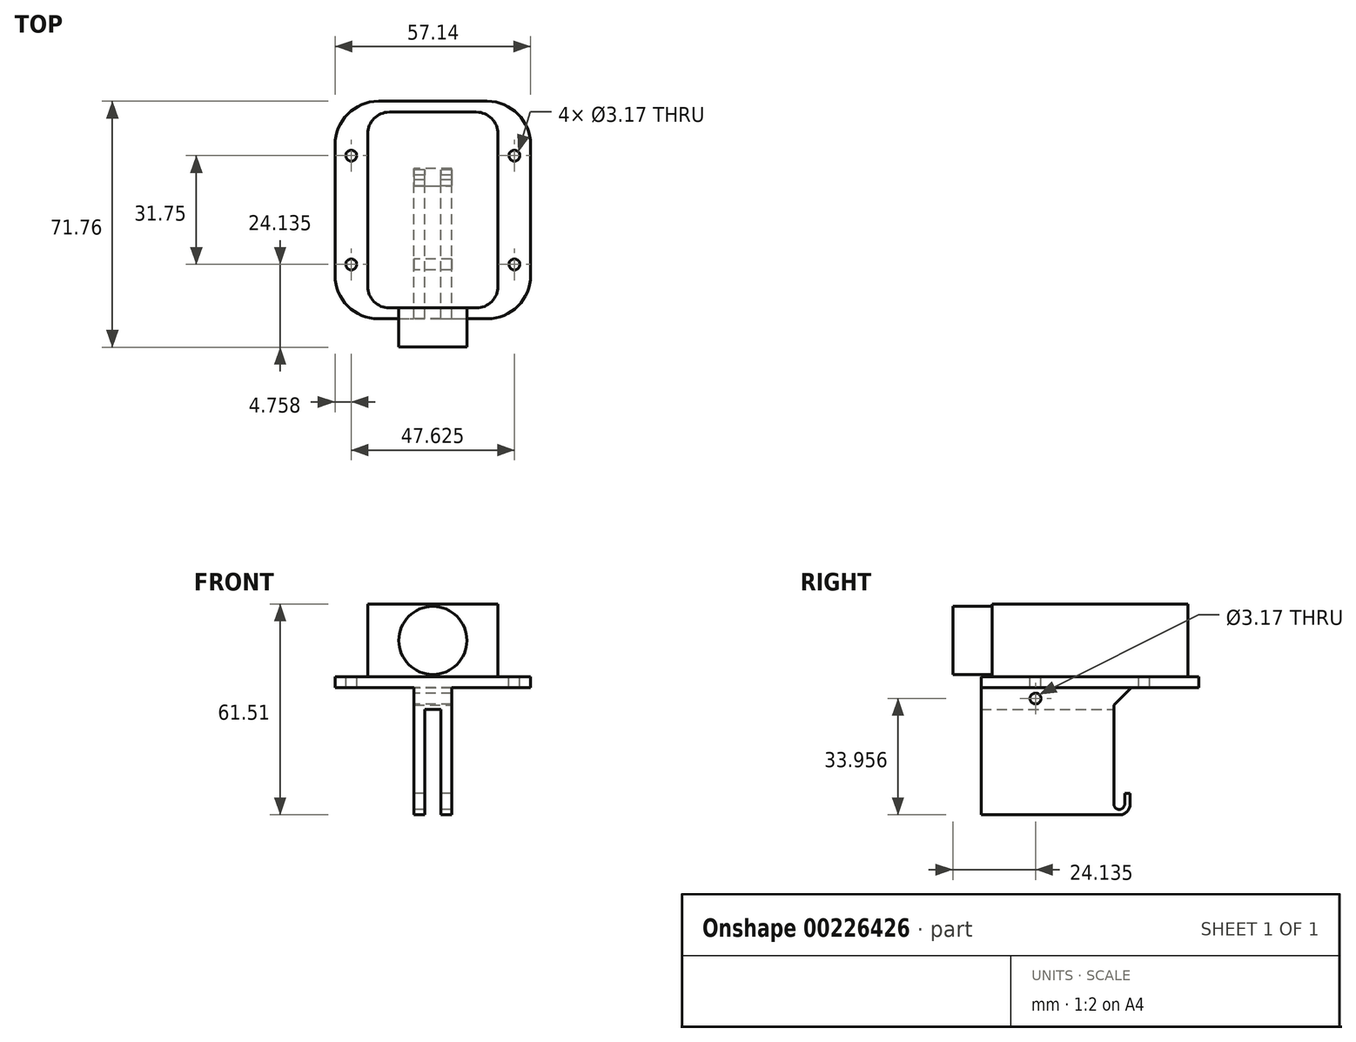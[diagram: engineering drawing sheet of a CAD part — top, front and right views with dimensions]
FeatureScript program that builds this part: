
annotation { "Feature Type Name" : "Feature", "Feature Type Description" : "" }
export const myFeature = defineFeature(function(context is Context, id is Id, definition is map)
    precondition{}
    {
        {
            var Q0;
            Q0=qCreatedBy(makeId("Top.planeOp"),FACE);
            var sketch = newSketch(context, id + "F0", { "sketchPlane" : qUnion([Q0])});
            skLineSegment(sketch, "E0.bottom", {"start": v(-12.7, 28.58) * mm, "end": v(12.7, 28.58) * mm});
            skLineSegment(sketch, "E0.top", {"start": v(-12.7, -28.58) * mm, "end": v(12.7, -28.58) * mm});
            skLineSegment(sketch, "E0.left", {"start": v(-19.05, 22.23) * mm, "end": v(-19.05, -22.23) * mm});
            skLineSegment(sketch, "E0.right", {"start": v(19.05, 22.23) * mm, "end": v(19.05, -22.23) * mm});
            skPoint(sketch, "E0.middle", {"position": v(0, 0) * mm});
            skPoint(sketch, "E1.visualSharp", {"position": v(-19.05, 28.58) * mm});
            skArc(sketch, "E1.filletArc", {"start": v(-12.7, 28.58) * mm, "mid": v(-17.2, 26.72) * mm, "end": v(-19.05, 22.23) * mm});
            skPoint(sketch, "E2.visualSharp", {"position": v(19.05, 28.58) * mm});
            skArc(sketch, "E2.filletArc", {"start": v(19.05, 22.23) * mm, "mid": v(17.2, 26.72) * mm, "end": v(12.7, 28.58) * mm});
            skPoint(sketch, "E3.visualSharp", {"position": v(19.05, -28.58) * mm});
            skArc(sketch, "E3.filletArc", {"start": v(12.7, -28.58) * mm, "mid": v(17.2, -26.72) * mm, "end": v(19.05, -22.23) * mm});
            skPoint(sketch, "E4.visualSharp", {"position": v(-19.05, -28.58) * mm});
            skArc(sketch, "E4.filletArc", {"start": v(-19.05, -22.23) * mm, "mid": v(-17.2, -26.72) * mm, "end": v(-12.7, -28.58) * mm});
            skCircle(sketch, "E5", {"center": v(0, 19.05) * mm, "radius": 4.76 * mm});
            skCircle(sketch, "E6", {"center": v(0, 8.57) * mm, "radius": 2.98 * mm});
            skSolve(sketch);
        }
        {
            var Q0;
            Q0 = qSketchRegion(id + "F0", true);
            var Q1;
            Q1=makeQuery(id+"F0.imprint","IMPRINT",FACE,{"disambiguationData":[TD([[makeQuery(id+"F0.imprint","IMPRINT",EDGE,{"derivedFrom":sQuery(id+"F0.wireOp",EDGE,"E5")}),1.0]])]});
            var Q2;
            Q2=makeQuery(id+"F0.imprint","IMPRINT",FACE,{"disambiguationData":[TD([[makeQuery(id+"F0.imprint","IMPRINT",EDGE,{"derivedFrom":sQuery(id+"F0.wireOp",EDGE,"E6")}),1.0]])]});
            extrude(context, id + "F1", {"entities" : qUnion([Q0, Q1, Q2]), "depth" : 21.2 * mm, "offsetDistance" : 25.4 * mm, "symmetric" : true});
        }
        {
            var Q0;
            Q0=makeQuery(id+"F1.opExtrude","SWEPT_FACE",FACE,{"disambiguationData":[OSD([sQuery(id+"F0.wireOp",EDGE,"E0.top")])]});
            var sketch = newSketch(context, id + "F2", { "sketchPlane" : qUnion([Q0])});
            skCircle(sketch, "E7", {"center": v(0, 0) * mm, "radius": 9.94 * mm});
            skSolve(sketch);
        }
        {
            var Q0;
            Q0 = qSketchRegion(id + "F2", true);
            extrude(context, id + "F3", {"entities" : qUnion([Q0]), "operationType" : NewBodyOperationType.ADD, "depth" : 11.43 * mm, "offsetDistance" : 25.4 * mm});
        }
        {
            var Q0;
            Q0=qCreatedBy(makeId("Front.planeOp"),FACE);
            var sketch = newSketch(context, id + "F4", { "sketchPlane" : qUnion([Q0])});
            skLineSegment(sketch, "E8.bottom", {"start": v(-2.29, -13.78) * mm, "end": v(2.29, -13.78) * mm});
            skLineSegment(sketch, "E8.left", {"start": v(-2.29, -13.78) * mm, "end": v(-2.29, -51.88) * mm});
            skLineSegment(sketch, "E8.right", {"start": v(2.29, -13.78) * mm, "end": v(2.29, -51.88) * mm});
            skPoint(sketch, "E8.middle", {"position": v(0, -32.83) * mm});
            skLineSegment(sketch, "E9.bottom", {"start": v(-28.57, -10.6) * mm, "end": v(28.57, -10.6) * mm});
            skLineSegment(sketch, "E9.top", {"start": v(-28.57, -13.78) * mm, "end": v(28.57, -13.78) * mm});
            skLineSegment(sketch, "E9.left", {"start": v(-28.57, -10.6) * mm, "end": v(-28.57, -13.78) * mm});
            skLineSegment(sketch, "E9.right", {"start": v(28.57, -10.6) * mm, "end": v(28.57, -13.78) * mm});
            skPoint(sketch, "E9.middle", {"position": v(0, -12.2) * mm});
            skSolve(sketch);
        }
        {
            var Q0;
            Q0 = qSketchRegion(id + "F4", true);
            extrude(context, id + "F5", {"entities" : qUnion([Q0]), "depth" : 63.5 * mm, "offsetDistance" : 25.4 * mm, "symmetric" : true});
        }
        {
            var Q0;
            Q0=makeQuery(id+"F5.opExtrude","SWEPT_FACE",FACE,{"disambiguationData":[OSD([sQuery(id+"F4.wireOp",EDGE,"E9.bottom")])]});
            var sketch = newSketch(context, id + "F6", { "sketchPlane" : qUnion([Q0])});
            skCircle(sketch, "E10", {"center": v(23.81, 15.88) * mm, "radius": 1.59 * mm});
            skLineSegment(sketch, "E11", {"start": v(28.57, 15.88) * mm, "end": v(19.05, 15.88) * mm, "construction": true});
            skCircle(sketch, "E12.MirrorC", {"center": v(-23.81, 15.88) * mm, "radius": 1.59 * mm});
            skCircle(sketch, "E13.MirrorC", {"center": v(-23.81, -15.88) * mm, "radius": 1.59 * mm});
            skCircle(sketch, "E14.MirrorC", {"center": v(23.81, -15.88) * mm, "radius": 1.59 * mm});
            skSolve(sketch);
        }
        {
            var Q0;
            Q0 = qSketchRegion(id + "F6", true);
            var Q1;
            Q1=makeQuery(id+"F5.opExtrude","SWEPT_FACE",FACE,{"disambiguationData":[OSD([sQuery(id+"F4.wireOp",EDGE,"E9.top")])]});
            extrude(context, id + "F7", {"entities" : qUnion([Q0]), "operationType" : NewBodyOperationType.REMOVE, "endBound" : BoundingType.UP_TO_SURFACE, "oppositeDirection" : true, "depth" : 25.4 * mm, "endBoundEntityFace" : qUnion([Q1]), "offsetDistance" : 25.4 * mm});
        }
        {
            var Q0;
            Q0=qCreatedBy(makeId("Front.planeOp"),FACE);
            var sketch = newSketch(context, id + "F8", { "sketchPlane" : qUnion([Q0])});
            skLineSegment(sketch, "E15.bottom", {"start": v(-2.29, -13.78) * mm, "end": v(2.29, -13.78) * mm});
            skLineSegment(sketch, "E15.left", {"start": v(-2.29, -13.78) * mm, "end": v(-2.29, -50.91) * mm});
            skLineSegment(sketch, "E15.right", {"start": v(2.29, -13.78) * mm, "end": v(2.29, -50.91) * mm});
            skPoint(sketch, "E15.middle", {"position": v(0, -32.35) * mm});
            skLineSegment(sketch, "E16.bottom", {"start": v(-2.29, -50.91) * mm, "end": v(-5.46, -50.91) * mm});
            skLineSegment(sketch, "E16.top", {"start": v(-2.29, -13.78) * mm, "end": v(-5.46, -13.78) * mm});
            skLineSegment(sketch, "E16.left", {"start": v(-2.29, -50.91) * mm, "end": v(-2.29, -13.78) * mm});
            skLineSegment(sketch, "E16.right", {"start": v(-5.46, -50.91) * mm, "end": v(-5.46, -13.78) * mm});
            skLineSegment(sketch, "E17.MirrorCS", {"start": v(5.46, -50.91) * mm, "end": v(5.46, -13.78) * mm});
            skLineSegment(sketch, "E18.MirrorCS", {"start": v(2.29, -50.91) * mm, "end": v(5.46, -50.91) * mm});
            skLineSegment(sketch, "E19.MirrorCS", {"start": v(2.29, -13.78) * mm, "end": v(5.46, -13.78) * mm});
            skLineSegment(sketch, "E20.bottom", {"start": v(5.46, -13.78) * mm, "end": v(-5.46, -13.78) * mm});
            skLineSegment(sketch, "E20.top", {"start": v(5.46, -20.13) * mm, "end": v(-5.46, -20.13) * mm});
            skLineSegment(sketch, "E20.left", {"start": v(5.46, -13.78) * mm, "end": v(5.46, -20.13) * mm});
            skLineSegment(sketch, "E20.right", {"start": v(-5.46, -13.78) * mm, "end": v(-5.46, -20.13) * mm});
            skPoint(sketch, "E20.middle", {"position": v(0, -16.95) * mm});
            skSolve(sketch);
        }
        {
            var Q0;
            Q0 = qSketchRegion(id + "F8", true);
            var Q1;
            Q1=makeQuery(id+"F5.opExtrude","CAP_FACE",FACE,{"disambiguationData":[OSD([sQuery(id+"F4.wireOp",EDGE,"E9.bottom"),sQuery(id+"F4.wireOp",EDGE,"E9.top"),sQuery(id+"F4.wireOp",EDGE,"E9.left"),sQuery(id+"F4.wireOp",EDGE,"E9.right")])],"isStart":false});
            extrude(context, id + "F9", {"entities" : qUnion([Q0]), "operationType" : NewBodyOperationType.ADD, "endBound" : BoundingType.UP_TO_SURFACE, "depth" : 34.92 * mm, "endBoundEntityFace" : qUnion([Q1]), "offsetDistance" : 25.4 * mm, "hasSecondDirection" : true, "secondDirectionOppositeDirection" : true, "secondDirectionDepth" : 12.7 * mm});
        }
        {
            var Q0;
            Q0=makeQuery(id+"F9.opExtrude","SWEPT_FACE",FACE,{"disambiguationData":[OSD([sQuery(id+"F8.wireOp",EDGE,"E16.right")])]});
            var sketch = newSketch(context, id + "F10", { "sketchPlane" : qUnion([Q0])});
            skLineSegment(sketch, "E21", {"start": v(-6.99, -20.13) * mm, "end": v(-6.99, -49.34) * mm});
            skArc(sketch, "E22", {"start": v(-10.16, -47.75) * mm, "mid": v(-8.57, -49.34) * mm, "end": v(-6.99, -47.75) * mm});
            skLineSegment(sketch, "E23", {"start": v(-6.99, -49.34) * mm, "end": v(-11.32, -49.34) * mm});
            skArc(sketch, "E24", {"start": v(-11.75, -47.75) * mm, "mid": v(-6.99, -50.5) * mm, "end": v(-6.99, -45) * mm});
            skLineSegment(sketch, "E25", {"start": v(-10.16, -47.75) * mm, "end": v(-10.16, -44.58) * mm});
            skLineSegment(sketch, "E26", {"start": v(-11.75, -47.75) * mm, "end": v(-11.75, -44.58) * mm});
            skLineSegment(sketch, "E27", {"start": v(-10.16, -44.58) * mm, "end": v(-11.75, -44.58) * mm});
            skLineSegment(sketch, "E28.0", {"start": v(-12.7, -50.91) * mm, "end": v(-12.7, -50.91) * mm});
            skLineSegment(sketch, "E29.0", {"start": v(31.75, -13.78) * mm, "end": v(-31.75, -13.78) * mm});
            skLineSegment(sketch, "E30", {"start": v(-6.99, -20.13) * mm, "end": v(-6.99, -13.78) * mm});
            skLineSegment(sketch, "E31.0", {"start": v(-12.7, -50.91) * mm, "end": v(-12.7, -13.78) * mm});
            skLineSegment(sketch, "E32.0", {"start": v(14.29, -10.6) * mm, "end": v(17.46, -10.6) * mm});
            skCircle(sketch, "E33", {"center": v(15.88, -16.95) * mm, "radius": 1.59 * mm});
            skPoint(sketch, "E33.centerSnap0", {"position": v(15.88, -10.6) * mm});
            skSolve(sketch);
        }
        {
            var Q0;
            {var subQ6=sQuery(id+"F10.wireOp",EDGE,"E25");Q0=makeQuery(id+"F10.imprint","IMPRINT",FACE,{"disambiguationData":[TD([[makeQuery(id+"F10.imprint","IMPRINT",EDGE,{"derivedFrom":subQ6}),-1.0]])]});}
            var Q1;
            Q1=makeQuery(id+"F10.imprint","IMPRINT",FACE,{"disambiguationData":[TD([[makeQuery(id+"F10.imprint","IMPRINT",EDGE,{"derivedFrom":sQuery(id+"F10.wireOp",EDGE,"E33")}),1.0]])]});
            var Q2;
            Q2=makeQuery(id+"F9.opExtrude","SWEPT_FACE",FACE,{"disambiguationData":[OSD([sQuery(id+"F8.wireOp",EDGE,"E17.MirrorCS")])]});
            extrude(context, id + "F11", {"entities" : qUnion([Q0, Q1]), "operationType" : NewBodyOperationType.REMOVE, "endBound" : BoundingType.UP_TO_SURFACE, "oppositeDirection" : true, "depth" : 25.4 * mm, "endBoundEntityFace" : qUnion([Q2]), "offsetDistance" : 25.4 * mm});
        }
        {
            var Q0;
            Q0=makeQuery(id+"F5.opExtrude","CAP_EDGE",EDGE,{"disambiguationData":[OSD([sQuery(id+"F4.wireOp",EDGE,"E9.left")])],"isStart":false});
            var Q1;
            Q1=makeQuery(id+"F5.opExtrude","CAP_EDGE",EDGE,{"disambiguationData":[OSD([sQuery(id+"F4.wireOp",EDGE,"E9.right")])],"isStart":false});
            var Q2;
            Q2=makeQuery(id+"F5.opExtrude","CAP_EDGE",EDGE,{"disambiguationData":[OSD([sQuery(id+"F4.wireOp",EDGE,"E9.right")])],"isStart":true});
            var Q3;
            Q3=makeQuery(id+"F5.opExtrude","CAP_EDGE",EDGE,{"disambiguationData":[OSD([sQuery(id+"F4.wireOp",EDGE,"E9.left")])],"isStart":true});
            var Q4;
            Q4=makeQuery(id+"F9.opExtrude","TWEAK_EDGE",EDGE,{"derivedFrom":[makeQuery(id+"F5.opExtrude","CAP_FACE",FACE,{"disambiguationData":[OSD([sQuery(id+"F4.wireOp",EDGE,"E9.bottom"),sQuery(id+"F4.wireOp",EDGE,"E9.top"),sQuery(id+"F4.wireOp",EDGE,"E9.left"),sQuery(id+"F4.wireOp",EDGE,"E9.right")])],"isStart":false}),makeQuery(id+"F8.imprint","IMPRINT",EDGE,{"derivedFrom":sQuery(id+"F8.wireOp",EDGE,"E16.bottom")})]});
            var Q5;
            Q5=makeQuery(id+"F9.opExtrude","TWEAK_EDGE",EDGE,{"derivedFrom":[makeQuery(id+"F5.opExtrude","CAP_FACE",FACE,{"disambiguationData":[OSD([sQuery(id+"F4.wireOp",EDGE,"E9.bottom"),sQuery(id+"F4.wireOp",EDGE,"E9.top"),sQuery(id+"F4.wireOp",EDGE,"E9.left"),sQuery(id+"F4.wireOp",EDGE,"E9.right")])],"isStart":false}),makeQuery(id+"F8.imprint","IMPRINT",EDGE,{"derivedFrom":sQuery(id+"F8.wireOp",EDGE,"E18.MirrorCS")})]});
            fillet(context, id + "F12", {"entities" : qUnion([Q0, Q1, Q2, Q3, Q4, Q5]), "radius" : 12.7 * mm, "tangentPropagation" : true, "allowEdgeOverflow" : false});
        }
        {
            var Q0;
            Q0=makeQuery(id+"F9.opExtrude","SWEPT_EDGE",EDGE,{"disambiguationData":[OSD([sQuery(id+"F8.wireOp",EDGE,"E20.bottom"),sQuery(id+"F8.wireOp",EDGE,"E20.right")])]});
            var Q1;
            Q1=makeQuery(id+"F11.boolean.opBoolean","COPY",EDGE,{"derivedFrom":makeQuery(id+"F11.opExtrude","SWEPT_EDGE",EDGE,{"disambiguationData":[OSD([sQuery(id+"F10.wireOp",EDGE,"E29.0"),sQuery(id+"F10.wireOp",EDGE,"E30")])]})});
            var Q2;
            Q2=makeQuery(id+"F9.opExtrude","SWEPT_EDGE",EDGE,{"disambiguationData":[OSD([sQuery(id+"F8.wireOp",EDGE,"E20.bottom"),sQuery(id+"F8.wireOp",EDGE,"E20.left")])]});
            chamfer(context, id + "F13", {"entities" : qUnion([Q0, Q1, Q2]), "width" : 5.08 * mm, "tangentPropagation" : true});
        }
    });
